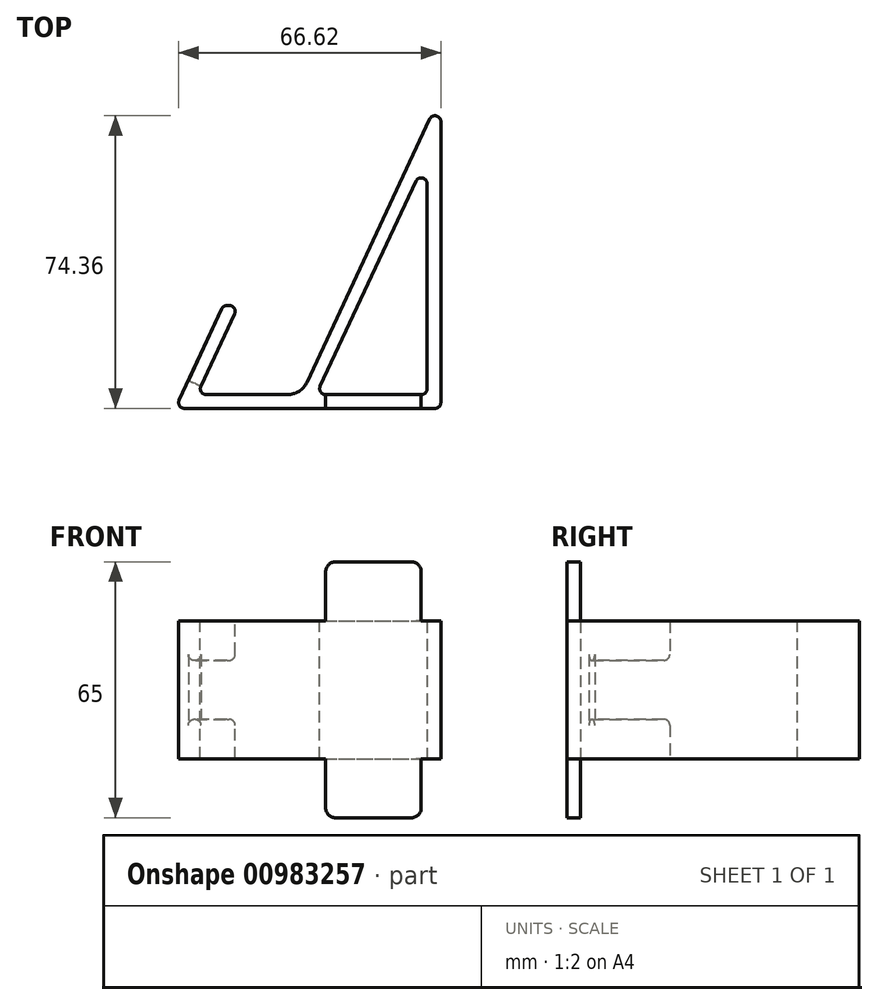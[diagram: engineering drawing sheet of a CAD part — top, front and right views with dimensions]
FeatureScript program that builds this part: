
annotation { "Feature Type Name" : "Feature", "Feature Type Description" : "" }
export const myFeature = defineFeature(function(context is Context, id is Id, definition is map)
    precondition{}
    {
        {
            assignVariable(context, id + "F0", {"name" : "Angle", "anyValue" : 65});
        }
        {
            assignVariable(context, id + "F1", {"name" : "ExtWidth", "anyValue" : 35});
        }
        {
            var Q0;
            Q0=qCreatedBy(makeId("Top.planeOp"),FACE);
            var sketch = newSketch(context, id + "F2", { "sketchPlane" : qUnion([Q0])});
            skLineSegment(sketch, "E0", {"start": v(-34.9, -1.47) * mm, "end": v(-45.47, -24.13) * mm});
            skLineSegment(sketch, "E1", {"start": v(-19, -24.13) * mm, "end": v(16.5, 52) * mm});
            skLineSegment(sketch, "E2", {"start": v(-34.9, -1.47) * mm, "end": v(-38.77, -1.47) * mm});
            skLineSegment(sketch, "E3", {"start": v(-38.77, -1.47) * mm, "end": v(-50.97, -27.63) * mm});
            skLineSegment(sketch, "E4", {"start": v(-50.97, -27.63) * mm, "end": v(16.5, -27.63) * mm});
            skLineSegment(sketch, "E5", {"start": v(-45.47, -24.13) * mm, "end": v(-19, -24.13) * mm});
            skLineSegment(sketch, "E6", {"start": v(16.5, 52) * mm, "end": v(16.5, -27.63) * mm});
            skLineSegment(sketch, "E7", {"start": v(-15.13, -24.13) * mm, "end": v(13, 36.21) * mm});
            skLineSegment(sketch, "E8", {"start": v(13, 36.21) * mm, "end": v(13, -24.13) * mm});
            skLineSegment(sketch, "E9", {"start": v(13, -24.13) * mm, "end": v(-15.13, -24.13) * mm});
            skSolve(sketch);
        }
        {
            var Q0;
            Q0=makeQuery(id+"F2.imprint","IMPRINT",FACE,{"disambiguationData":[TD([[makeQuery(id+"F2.imprint","IMPRINT",EDGE,{"derivedFrom":sQuery(id+"F2.wireOp",EDGE,"E0")}),-1.0]])]});
            extrude(context, id + "F3", {"entities" : qUnion([Q0]), "endBound" : BoundingType.SYMMETRIC, "depth" : (getVariable(context, 'ExtWidth')) * mm, "offsetDistance" : 25 * mm});
        }
        {
            var Q0;
            Q0=makeQuery(id+"F3.opExtrude","SWEPT_EDGE",EDGE,{"disambiguationData":[OSD([sQuery(id+"F2.wireOp",EDGE,"E1"),sQuery(id+"F2.wireOp",EDGE,"E6")])]});
            var Q1;
            Q1=makeQuery(id+"F3.opExtrude","SWEPT_EDGE",EDGE,{"disambiguationData":[OSD([sQuery(id+"F2.wireOp",EDGE,"E7"),sQuery(id+"F2.wireOp",EDGE,"E8")])]});
            var Q2;
            Q2=makeQuery(id+"F3.opExtrude","SWEPT_EDGE",EDGE,{"disambiguationData":[OSD([sQuery(id+"F2.wireOp",EDGE,"E8"),sQuery(id+"F2.wireOp",EDGE,"E9")])]});
            var Q3;
            Q3=makeQuery(id+"F3.opExtrude","SWEPT_EDGE",EDGE,{"disambiguationData":[OSD([sQuery(id+"F2.wireOp",EDGE,"E4"),sQuery(id+"F2.wireOp",EDGE,"E6")])]});
            var Q4;
            Q4=makeQuery(id+"F3.opExtrude","SWEPT_EDGE",EDGE,{"disambiguationData":[OSD([sQuery(id+"F2.wireOp",EDGE,"E7"),sQuery(id+"F2.wireOp",EDGE,"E9")])]});
            var Q5;
            Q5=makeQuery(id+"F3.opExtrude","SWEPT_EDGE",EDGE,{"disambiguationData":[OSD([sQuery(id+"F2.wireOp",EDGE,"E0"),sQuery(id+"F2.wireOp",EDGE,"E5")])]});
            var Q6;
            Q6=makeQuery(id+"F3.opExtrude","SWEPT_EDGE",EDGE,{"disambiguationData":[OSD([sQuery(id+"F2.wireOp",EDGE,"E3"),sQuery(id+"F2.wireOp",EDGE,"E4")])]});
            var Q7;
            Q7=makeQuery(id+"F3.opExtrude","SWEPT_EDGE",EDGE,{"disambiguationData":[OSD([sQuery(id+"F2.wireOp",EDGE,"E2"),sQuery(id+"F2.wireOp",EDGE,"E3")])]});
            var Q8;
            Q8=makeQuery(id+"F3.opExtrude","SWEPT_EDGE",EDGE,{"disambiguationData":[OSD([sQuery(id+"F2.wireOp",EDGE,"E0"),sQuery(id+"F2.wireOp",EDGE,"E2")])]});
            fillet(context, id + "F4", {"entities" : qUnion([Q0, Q1, Q2, Q3, Q4, Q5, Q6, Q7, Q8]), "radius" : 1.5 * mm, "tangentPropagation" : true, "allowEdgeOverflow" : false});
        }
        {
            var Q0;
            Q0=makeQuery(id+"F3.opExtrude","SWEPT_EDGE",EDGE,{"disambiguationData":[OSD([sQuery(id+"F2.wireOp",EDGE,"E1"),sQuery(id+"F2.wireOp",EDGE,"E5")])]});
            fillet(context, id + "F5", {"entities" : qUnion([Q0]), "radius" : (getVariable(context, 'Angle') / 12) * mm, "tangentPropagation" : true, "allowEdgeOverflow" : false});
        }
        {
            var Q0;
            Q0=makeQuery(id+"F3.opExtrude","SWEPT_FACE",FACE,{"disambiguationData":[OSD([sQuery(id+"F2.wireOp",EDGE,"E3")])]});
            var sketch = newSketch(context, id + "F6", { "sketchPlane" : qUnion([Q0])});
            skLineSegment(sketch, "E10", {"start": v(18.67, 0) * mm, "end": v(61.52, 0) * mm, "construction": true});
            skLineSegment(sketch, "E11", {"start": v(15.81, 7.5) * mm, "end": v(38.73, 7.5) * mm});
            skLineSegment(sketch, "E12.MirrorCS", {"start": v(15.81, -7.5) * mm, "end": v(38.73, -7.5) * mm});
            skLineSegment(sketch, "E13", {"start": v(15.81, 7.5) * mm, "end": v(15.81, -7.5) * mm});
            skLineSegment(sketch, "E14", {"start": v(38.73, 7.5) * mm, "end": v(38.73, -7.5) * mm});
            skSolve(sketch);
        }
        {
            var Q0;
            {var subQ0=sQuery(id+"F6.wireOp",EDGE,"E14");Q0=makeQuery(id+"F6.imprint","IMPRINT",FACE,{"disambiguationData":[TD([[makeQuery(id+"F6.imprint","IMPRINT",EDGE,{"derivedFrom":subQ0}),-1.0]])]});}
            var Q1;
            {var subQ0=sQuery(id+"F6.wireOp",EDGE,"E13");Q1=makeQuery(id+"F6.imprint","IMPRINT",FACE,{"disambiguationData":[TD([[makeQuery(id+"F6.imprint","IMPRINT",EDGE,{"derivedFrom":subQ0}),1.0]])]});}
            extrude(context, id + "F7", {"entities" : qUnion([Q0, Q1]), "operationType" : NewBodyOperationType.REMOVE, "oppositeDirection" : true, "depth" : 3.6 * mm, "offsetDistance" : 25 * mm});
        }
        {
            var Q0;
            Q0=makeQuery(id+"F7.boolean.opBoolean","COPY",EDGE,{"derivedFrom":makeQuery(id+"F7.opExtrude","CAP_EDGE",EDGE,{"disambiguationData":[OSD([sQuery(id+"F6.wireOp",EDGE,"E14")])],"isStart":true})});
            var Q1;
            {var subQ0=sQuery(id+"F2.wireOp",EDGE,"E5");var subQ1=sQuery(id+"F2.wireOp",EDGE,"E0");Q1=makeQuery(id+"F7.boolean.opBoolean","SPLIT",EDGE,{"disambiguationData":[topologyDisambiguationEdgeConnected([makeQuery(id+"F4.opFillet","BLEND_FACE",FACE,{"disambiguationData":[OSD([subQ1,subQ0])]}),makeQuery(id+"F7.opExtrude","SWEPT_FACE",FACE,{"disambiguationData":[OSD([sQuery(id+"F6.wireOp",EDGE,"E14")])]})])],"derivedFrom":makeQuery(id+"F4.opFillet","BLEND_EDGE",EDGE,{"blendedFrom":[makeQuery(id+"F3.opExtrude","SWEPT_EDGE",EDGE,{"disambiguationData":[OSD([subQ1,subQ0])]}),makeQuery(id+"F3.opExtrude","SWEPT_FACE",FACE,{"disambiguationData":[OSD([subQ1])]})],"blendedInto":[makeQuery(id+"F3.opExtrude","SWEPT_FACE",FACE,{"disambiguationData":[OSD([subQ1])]})]})});}
            var Q2;
            Q2=makeQuery(id+"F7.boolean.opBoolean","COPY",EDGE,{"derivedFrom":makeQuery(id+"F7.opExtrude","CAP_EDGE",EDGE,{"disambiguationData":[OSD([sQuery(id+"F6.wireOp",EDGE,"E12.MirrorCS")])],"isStart":true})});
            var Q3;
            Q3=makeQuery(id+"F7.boolean.opBoolean","INTERSECT",EDGE,{"derivedFrom":[makeQuery(id+"F3.opExtrude","SWEPT_FACE",FACE,{"disambiguationData":[OSD([sQuery(id+"F2.wireOp",EDGE,"E0")])]}),makeQuery(id+"F7.opExtrude","SWEPT_FACE",FACE,{"disambiguationData":[OSD([sQuery(id+"F6.wireOp",EDGE,"E12.MirrorCS")])]})]});
            var Q4;
            Q4=makeQuery(id+"F7.boolean.opBoolean","COPY",EDGE,{"derivedFrom":makeQuery(id+"F7.opExtrude","CAP_EDGE",EDGE,{"disambiguationData":[OSD([sQuery(id+"F6.wireOp",EDGE,"E11")])],"isStart":true})});
            var Q5;
            Q5=makeQuery(id+"F7.boolean.opBoolean","INTERSECT",EDGE,{"derivedFrom":[makeQuery(id+"F3.opExtrude","SWEPT_FACE",FACE,{"disambiguationData":[OSD([sQuery(id+"F2.wireOp",EDGE,"E0")])]}),makeQuery(id+"F7.opExtrude","SWEPT_FACE",FACE,{"disambiguationData":[OSD([sQuery(id+"F6.wireOp",EDGE,"E11")])]})]});
            fillet(context, id + "F8", {"entities" : qUnion([Q0, Q1, Q2, Q3, Q4, Q5]), "radius" : 1.5 * mm, "tangentPropagation" : true, "allowEdgeOverflow" : false});
        }
        {
            var Q0;
            Q0=makeQuery(id+"F3.opExtrude","CAP_FACE",FACE,{"disambiguationData":[OSD([sQuery(id+"F2.wireOp",EDGE,"E0"),sQuery(id+"F2.wireOp",EDGE,"E1"),sQuery(id+"F2.wireOp",EDGE,"E2"),sQuery(id+"F2.wireOp",EDGE,"E3"),sQuery(id+"F2.wireOp",EDGE,"E4"),sQuery(id+"F2.wireOp",EDGE,"E5"),sQuery(id+"F2.wireOp",EDGE,"E6"),sQuery(id+"F2.wireOp",EDGE,"E7"),sQuery(id+"F2.wireOp",EDGE,"E8"),sQuery(id+"F2.wireOp",EDGE,"E9")])],"isStart":false});
            var sketch = newSketch(context, id + "F9", { "sketchPlane" : qUnion([Q0])});
            skLineSegment(sketch, "E15", {"start": v(11.5, -24.13) * mm, "end": v(11.5, -27.63) * mm});
            skLineSegment(sketch, "E16", {"start": v(-12.78, -24.13) * mm, "end": v(-12.78, -27.63) * mm});
            skSolve(sketch);
        }
        {
            var Q0;
            Q0=makeQuery(id+"F3.opExtrude","CAP_FACE",FACE,{"disambiguationData":[OSD([sQuery(id+"F2.wireOp",EDGE,"E0"),sQuery(id+"F2.wireOp",EDGE,"E1"),sQuery(id+"F2.wireOp",EDGE,"E2"),sQuery(id+"F2.wireOp",EDGE,"E3"),sQuery(id+"F2.wireOp",EDGE,"E4"),sQuery(id+"F2.wireOp",EDGE,"E5"),sQuery(id+"F2.wireOp",EDGE,"E6"),sQuery(id+"F2.wireOp",EDGE,"E7"),sQuery(id+"F2.wireOp",EDGE,"E8"),sQuery(id+"F2.wireOp",EDGE,"E9")])],"isStart":true});
            var sketch = newSketch(context, id + "F10", { "sketchPlane" : qUnion([Q0])});
            skLineSegment(sketch, "E17", {"start": v(-12.78, 24.13) * mm, "end": v(-12.78, 27.63) * mm});
            skLineSegment(sketch, "E18", {"start": v(11.5, 24.13) * mm, "end": v(11.5, 27.63) * mm});
            skSolve(sketch);
        }
        {
            var Q0;
            {var subQ0=sQuery(id+"F10.wireOp",EDGE,"E17");Q0=makeQuery(id+"F10.imprint","IMPRINT",FACE,{"disambiguationData":[TD([[makeQuery(id+"F10.imprint","IMPRINT",EDGE,{"derivedFrom":subQ0}),-1.0]])]});}
            extrude(context, id + "F11", {"entities" : qUnion([Q0]), "operationType" : NewBodyOperationType.ADD, "depth" : 15 * mm, "offsetDistance" : 25 * mm});
        }
        {
            var Q0;
            {var subQ0=sQuery(id+"F9.wireOp",EDGE,"E15");Q0=makeQuery(id+"F9.imprint","IMPRINT",FACE,{"disambiguationData":[TD([[makeQuery(id+"F9.imprint","IMPRINT",EDGE,{"derivedFrom":subQ0}),-1.0]])]});}
            extrude(context, id + "F12", {"entities" : qUnion([Q0]), "operationType" : NewBodyOperationType.ADD, "depth" : 15 * mm, "offsetDistance" : 25 * mm});
        }
        {
            var Q0;
            Q0=makeQuery(id+"F12.opExtrude","CAP_EDGE",EDGE,{"disambiguationData":[OSD([sQuery(id+"F9.wireOp",EDGE,"E16")])],"isStart":true});
            var Q1;
            Q1=makeQuery(id+"F12.opExtrude","CAP_EDGE",EDGE,{"disambiguationData":[OSD([sQuery(id+"F9.wireOp",EDGE,"E16")])],"isStart":false});
            var Q2;
            Q2=makeQuery(id+"F12.opExtrude","CAP_EDGE",EDGE,{"disambiguationData":[OSD([sQuery(id+"F9.wireOp",EDGE,"E15")])],"isStart":false});
            var Q3;
            Q3=makeQuery(id+"F12.opExtrude","CAP_EDGE",EDGE,{"disambiguationData":[OSD([sQuery(id+"F9.wireOp",EDGE,"E15")])],"isStart":true});
            var Q4;
            Q4=makeQuery(id+"F11.opExtrude","CAP_EDGE",EDGE,{"disambiguationData":[OSD([sQuery(id+"F10.wireOp",EDGE,"E18")])],"isStart":true});
            var Q5;
            Q5=makeQuery(id+"F11.opExtrude","CAP_EDGE",EDGE,{"disambiguationData":[OSD([sQuery(id+"F10.wireOp",EDGE,"E18")])],"isStart":false});
            var Q6;
            Q6=makeQuery(id+"F11.opExtrude","CAP_EDGE",EDGE,{"disambiguationData":[OSD([sQuery(id+"F10.wireOp",EDGE,"E17")])],"isStart":false});
            var Q7;
            Q7=makeQuery(id+"F11.opExtrude","CAP_EDGE",EDGE,{"disambiguationData":[OSD([sQuery(id+"F10.wireOp",EDGE,"E17")])],"isStart":true});
            fillet(context, id + "F13", {"entities" : qUnion([Q0, Q1, Q2, Q3, Q4, Q5, Q6, Q7]), "radius" : 2.5 * mm, "tangentPropagation" : true, "allowEdgeOverflow" : false});
        }
    });
